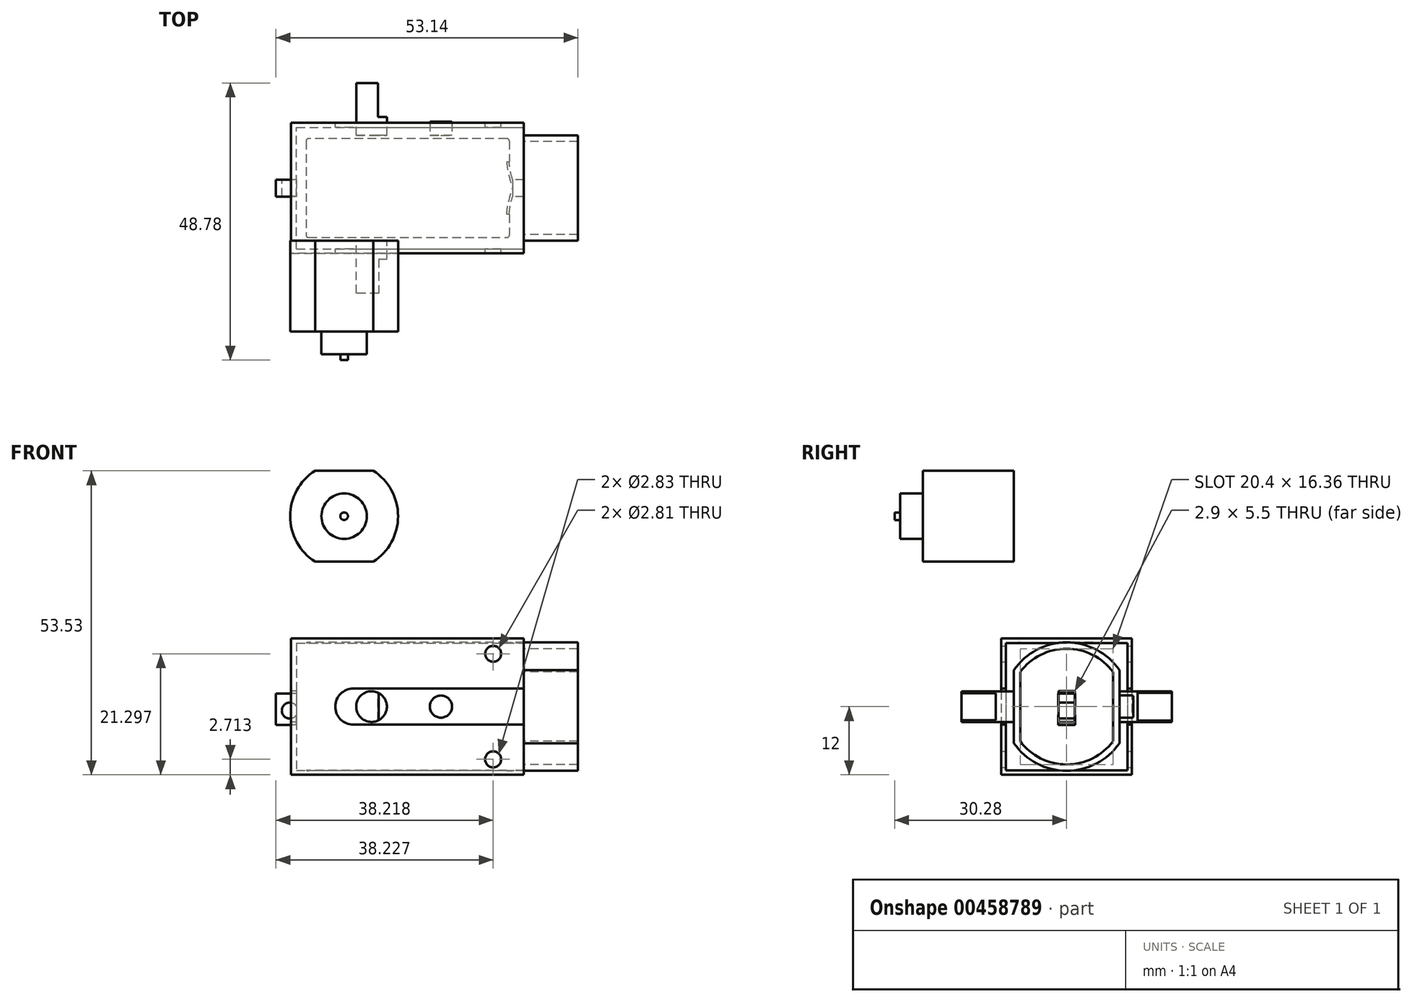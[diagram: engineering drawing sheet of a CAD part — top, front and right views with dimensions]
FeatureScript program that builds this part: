
annotation { "Feature Type Name" : "Feature", "Feature Type Description" : "" }
export const myFeature = defineFeature(function(context is Context, id is Id, definition is map)
    precondition{}
    {
        {
            var Q0;
            Q0=qCreatedBy(makeId("Front.planeOp"),FACE);
            var sketch = newSketch(context, id + "F0", { "sketchPlane" : qUnion([Q0])});
            skLineSegment(sketch, "E0.bottom", {"start": v(-10.04, -11.3) * mm, "end": v(-46.94, -11.3) * mm});
            skLineSegment(sketch, "E0.top", {"start": v(-10.04, 11.3) * mm, "end": v(-46.94, 11.3) * mm});
            skLineSegment(sketch, "E0.right", {"start": v(-46.94, -11.3) * mm, "end": v(-46.94, 11.3) * mm});
            skPoint(sketch, "E0.middle", {"position": v(-20.83, 0) * mm});
            skPoint(sketch, "E1.middle", {"position": v(8.58, 0) * mm});
            skCircle(sketch, "E2", {"center": v(-34.86, 0) * mm, "radius": 2.7 * mm});
            skLineSegment(sketch, "E3.bottom", {"start": v(-46.94, -3.26) * mm, "end": v(-51.68, -3.26) * mm});
            skLineSegment(sketch, "E3.top", {"start": v(-46.94, 2.31) * mm, "end": v(-51.68, 2.31) * mm});
            skLineSegment(sketch, "E3.left", {"start": v(-46.94, -3.26) * mm, "end": v(-46.94, 2.31) * mm});
            skLineSegment(sketch, "E3.right", {"start": v(-51.68, -3.26) * mm, "end": v(-51.68, 2.31) * mm});
            skCircle(sketch, "E4", {"center": v(-49.25, -0.7) * mm, "radius": 1.4 * mm});
            skLineSegment(sketch, "E5", {"start": v(-10.04, 11.3) * mm, "end": v(-10.04, -11.3) * mm});
            skPoint(sketch, "E6.orphan", {"position": v(5.29, 11.3) * mm});
            skPoint(sketch, "E7.orphan", {"position": v(5.29, -11.3) * mm});
            skCircle(sketch, "E8", {"center": v(-13.3, 8.7) * mm, "radius": 1.4 * mm});
            skCircle(sketch, "E9.MirrorC", {"center": v(-13.3, -8.7) * mm, "radius": 1.4 * mm});
            skSolve(sketch);
        }
        {
            var Q0;
            {var subQ9=sQuery(id+"F0.wireOp",EDGE,"E0.bottom");Q0=makeQuery(id+"F0.imprint","IMPRINT",FACE,{"disambiguationData":[TD([[makeQuery(id+"F0.imprint","IMPRINT",EDGE,{"derivedFrom":subQ9}),-1.0]])]});}
            var Q1;
            {var subQ5=sQuery(id+"F0.wireOp",EDGE,"E1.left");Q1=makeQuery(id+"F0.imprint","IMPRINT",FACE,{"disambiguationData":[TD([[makeQuery(id+"F0.imprint","IMPRINT",EDGE,{"derivedFrom":subQ5}),1.0]])]});}
            var Q2;
            {var subQ5=sQuery(id+"F0.wireOp",EDGE,"E1.right");Q2=makeQuery(id+"F0.imprint","IMPRINT",FACE,{"disambiguationData":[TD([[makeQuery(id+"F0.imprint","IMPRINT",EDGE,{"derivedFrom":subQ5}),-1.0]])]});}
            extrude(context, id + "F1", {"entities" : qUnion([Q0, Q1, Q2]), "depth" : 18.56 * mm, "symmetric" : true});
        }
        {
            var Q0;
            Q0=makeQuery(id+"F1.opExtrude","SWEPT_FACE",FACE,{"disambiguationData":[OSD([sQuery(id+"F0.wireOp",EDGE,"E5")])]});
            var sketch = newSketch(context, id + "F2", { "sketchPlane" : qUnion([Q0])});
            skArc(sketch, "E10", {"start": v(-9.28, -6.45) * mm, "mid": v(0, -11.3) * mm, "end": v(9.28, -6.45) * mm});
            skLineSegment(sketch, "E11.0", {"start": v(-9.28, 6.45) * mm, "end": v(-9.28, -6.45) * mm});
            skLineSegment(sketch, "E11.1", {"start": v(9.28, 6.45) * mm, "end": v(9.28, -6.45) * mm});
            skArc(sketch, "E12.trimOffspring", {"start": v(9.28, 6.45) * mm, "mid": v(0, 11.3) * mm, "end": v(-9.28, 6.45) * mm});
            skPoint(sketch, "E13.orphan", {"position": v(-9.28, 11.3) * mm});
            skPoint(sketch, "E14.orphan", {"position": v(-9.28, -11.3) * mm});
            skPoint(sketch, "E15.orphan", {"position": v(9.28, -11.3) * mm});
            skPoint(sketch, "E16.orphan", {"position": v(9.28, 11.3) * mm});
            skArc(sketch, "E17.0", {"start": v(8.18, 6.1) * mm, "mid": v(0, 10.2) * mm, "end": v(-8.18, 6.1) * mm});
            skLineSegment(sketch, "E17.1", {"start": v(8.18, 6.1) * mm, "end": v(8.18, -6.1) * mm});
            skArc(sketch, "E17.2", {"start": v(-8.18, -6.1) * mm, "mid": v(0, -10.2) * mm, "end": v(8.18, -6.1) * mm});
            skLineSegment(sketch, "E17.3", {"start": v(-8.18, 6.1) * mm, "end": v(-8.18, -6.1) * mm});
            skSolve(sketch);
        }
        {
            var Q0;
            {var subQ1=sQuery(id+"F2.wireOp",EDGE,"E11.0");Q0=makeQuery(id+"F2.imprint","IMPRINT",FACE,{"disambiguationData":[TD([[makeQuery(id+"F2.imprint","IMPRINT",EDGE,{"derivedFrom":subQ1}),1.0]])]});}
            extrude(context, id + "F3", {"entities" : qUnion([Q0]), "operationType" : NewBodyOperationType.ADD, "depth" : 11.5 * mm});
        }
        {
            var Q0;
            Q0=makeQuery(id+"F0.imprint","IMPRINT",FACE,{"disambiguationData":[TD([[makeQuery(id+"F0.imprint","IMPRINT",EDGE,{"derivedFrom":sQuery(id+"F0.wireOp",EDGE,"E3.bottom")}),-1.0]])]});
            extrude(context, id + "F4", {"entities" : qUnion([Q0]), "operationType" : NewBodyOperationType.ADD, "depth" : 3 * mm, "offsetDistance" : 25 * mm, "symmetric" : true});
        }
        {
            var Q0;
            Q0=makeQuery(id+"F0.imprint","IMPRINT",FACE,{"disambiguationData":[TD([[makeQuery(id+"F0.imprint","IMPRINT",EDGE,{"derivedFrom":sQuery(id+"F0.wireOp",EDGE,"E2")}),1.0]])]});
            extrude(context, id + "F5", {"entities" : qUnion([Q0]), "depth" : 37 * mm, "symmetric" : true});
        }
        {
            var Q0;
            Q0=makeQuery(id+"F5.opExtrude","CAP_FACE",FACE,{"disambiguationData":[OSD([sQuery(id+"F0.wireOp",EDGE,"E2")])],"isStart":false});
            var sketch = newSketch(context, id + "F6", { "sketchPlane" : qUnion([Q0])});
            skCircle(sketch, "E18.0.0", {"center": v(-34.86, 0) * mm, "radius": 2.7 * mm});
            skLineSegment(sketch, "E19", {"start": v(-33.6, 2.39) * mm, "end": v(-33.6, -2.39) * mm});
            skSolve(sketch);
        }
        {
            var Q0;
            {var subQ0=sQuery(id+"F6.wireOp",EDGE,"E19");Q0=makeQuery(id+"F6.imprint","IMPRINT",FACE,{"disambiguationData":[TD([[makeQuery(id+"F6.imprint","IMPRINT",EDGE,{"derivedFrom":subQ0}),1.0]])]});}
            extrude(context, id + "F7", {"entities" : qUnion([Q0]), "operationType" : NewBodyOperationType.REMOVE, "oppositeDirection" : true, "depth" : 6 * mm});
        }
        {
            var Q0;
            Q0=makeQuery(id+"F5.opExtrude","CAP_FACE",FACE,{"disambiguationData":[OSD([sQuery(id+"F0.wireOp",EDGE,"E2")])],"isStart":true});
            var sketch = newSketch(context, id + "F8", { "sketchPlane" : qUnion([Q0])});
            skLineSegment(sketch, "E20", {"start": v(33.7, -2.44) * mm, "end": v(33.7, 2.44) * mm});
            skSolve(sketch);
        }
        {
            var Q0;
            {var subQ0=sQuery(id+"F8.wireOp",EDGE,"E20");Q0=makeQuery(id+"F8.imprint","IMPRINT",FACE,{"disambiguationData":[TD([[makeQuery(id+"F8.imprint","IMPRINT",EDGE,{"derivedFrom":subQ0}),1.0]])]});}
            extrude(context, id + "F9", {"entities" : qUnion([Q0]), "operationType" : NewBodyOperationType.REMOVE, "oppositeDirection" : true, "depth" : 6 * mm});
        }
        {
            var Q0;
            Q0=makeQuery(id+"F3.boolean.opBoolean","MERGE",FACE,{"derivedFrom":[makeQuery(id+"F1.opExtrude","CAP_FACE",FACE,{"disambiguationData":[OSD([sQuery(id+"F0.wireOp",EDGE,"E0.bottom"),sQuery(id+"F0.wireOp",EDGE,"E0.top"),sQuery(id+"F0.wireOp",EDGE,"E0.right"),sQuery(id+"F0.wireOp",EDGE,"E2"),sQuery(id+"F0.wireOp",EDGE,"E3.left"),sQuery(id+"F0.wireOp",EDGE,"E5"),sQuery(id+"F0.wireOp",EDGE,"E8"),sQuery(id+"F0.wireOp",EDGE,"E9.MirrorC")])],"isStart":false}),makeQuery(id+"F3.opExtrude","SWEPT_FACE",FACE,{"disambiguationData":[OSD([sQuery(id+"F2.wireOp",EDGE,"E11.0")])]})]});
            var sketch = newSketch(context, id + "F10", { "sketchPlane" : qUnion([Q0])});
            skArc(sketch, "E21", {"start": v(-44.8, 41.53) * mm, "mid": v(-49.18, 33.53) * mm, "end": v(-44.8, 25.53) * mm});
            skLineSegment(sketch, "E22.bottom", {"start": v(-44.8, 41.53) * mm, "end": v(-34.56, 41.53) * mm});
            skLineSegment(sketch, "E22.top", {"start": v(-44.8, 25.53) * mm, "end": v(-34.56, 25.53) * mm});
            skArc(sketch, "E23.trimOffspring", {"start": v(-34.56, 25.53) * mm, "mid": v(-30.18, 33.53) * mm, "end": v(-34.56, 41.53) * mm});
            skSolve(sketch);
        }
        {
            var Q0;
            Q0=qSketchRegion(id+"F10",true);
            extrude(context, id + "F11", {"entities" : qUnion([Q0]), "depth" : 16 * mm});
        }
        {
            var Q0;
            Q0=makeQuery(id+"F11.opExtrude","CAP_FACE",FACE,{"disambiguationData":[OSD([sQuery(id+"F10.wireOp",EDGE,"E21"),sQuery(id+"F10.wireOp",EDGE,"E22.bottom"),sQuery(id+"F10.wireOp",EDGE,"E22.top"),sQuery(id+"F10.wireOp",EDGE,"E23.trimOffspring")])],"isStart":false});
            var sketch = newSketch(context, id + "F12", { "sketchPlane" : qUnion([Q0])});
            skCircle(sketch, "E24", {"center": v(-39.68, 33.53) * mm, "radius": 4 * mm});
            skCircle(sketch, "E25", {"center": v(-39.68, 33.53) * mm, "radius": 0.67 * mm});
            skSolve(sketch);
        }
        {
            var Q0;
            Q0=makeQuery(id+"F12.imprint","IMPRINT",FACE,{"disambiguationData":[TD([[makeQuery(id+"F12.imprint","IMPRINT",EDGE,{"derivedFrom":sQuery(id+"F12.wireOp",EDGE,"E24")}),1.0]])]});
            extrude(context, id + "F13", {"entities" : qUnion([Q0]), "operationType" : NewBodyOperationType.ADD, "depth" : 4 * mm});
        }
        {
            var Q0;
            Q0=makeQuery(id+"F13.boolean.opBoolean","SPLIT",FACE,{"disambiguationData":[TD([makeQuery(id+"F13.opExtrude","SWEPT_FACE",FACE,{"disambiguationData":[OSD([sQuery(id+"F12.wireOp",EDGE,"E25")])]})])],"derivedFrom":makeQuery(id+"F11.opExtrude","CAP_FACE",FACE,{"disambiguationData":[OSD([sQuery(id+"F10.wireOp",EDGE,"E21"),sQuery(id+"F10.wireOp",EDGE,"E22.bottom"),sQuery(id+"F10.wireOp",EDGE,"E22.top"),sQuery(id+"F10.wireOp",EDGE,"E23.trimOffspring")])],"isStart":false})});
            extrude(context, id + "F14", {"entities" : qUnion([Q0]), "operationType" : NewBodyOperationType.ADD, "depth" : 5 * mm});
        }
        {
            var Q0;
            Q0=makeQuery(id+"F1.opExtrude","CAP_EDGE",EDGE,{"disambiguationData":[OSD([sQuery(id+"F0.wireOp",EDGE,"E0.top")])],"isStart":false});
            var Q1;
            {var subQ0=sQuery(id+"F0.wireOp",EDGE,"E5");var subQ1=sQuery(id+"F0.wireOp",EDGE,"E0.top");Q1=makeQuery(id+"F3.boolean.opBoolean","SPLIT",EDGE,{"disambiguationData":[TD([makeQuery(id+"F3.opExtrude","SWEPT_FACE",FACE,{"disambiguationData":[OSD([sQuery(id+"F2.wireOp",EDGE,"E11.0")])]})])],"derivedFrom":makeQuery(id+"F1.opExtrude","SWEPT_EDGE",EDGE,{"disambiguationData":[OSD([subQ1,subQ0])]})});}
            var Q2;
            {var subQ0=sQuery(id+"F0.wireOp",EDGE,"E0.top");var subQ1=sQuery(id+"F0.wireOp",EDGE,"E5");Q2=makeQuery(id+"F3.boolean.opBoolean","SPLIT",EDGE,{"disambiguationData":[TD([makeQuery(id+"F3.opExtrude","SWEPT_FACE",FACE,{"disambiguationData":[OSD([sQuery(id+"F2.wireOp",EDGE,"E11.1")])]})])],"derivedFrom":makeQuery(id+"F1.opExtrude","SWEPT_EDGE",EDGE,{"disambiguationData":[OSD([subQ0,subQ1])]})});}
            var Q3;
            Q3=makeQuery(id+"F1.opExtrude","CAP_EDGE",EDGE,{"disambiguationData":[OSD([sQuery(id+"F0.wireOp",EDGE,"E0.top")])],"isStart":true});
            var Q4;
            Q4=makeQuery(id+"F1.opExtrude","SWEPT_EDGE",EDGE,{"disambiguationData":[OSD([sQuery(id+"F0.wireOp",EDGE,"E0.top"),sQuery(id+"F0.wireOp",EDGE,"E0.right")])]});
            var Q5;
            Q5=makeQuery(id+"F1.opExtrude","CAP_EDGE",EDGE,{"disambiguationData":[OSD([sQuery(id+"F0.wireOp",EDGE,"E0.right"),sQuery(id+"F0.wireOp",EDGE,"E3.left")])],"isStart":true});
            var Q6;
            Q6=makeQuery(id+"F1.opExtrude","CAP_EDGE",EDGE,{"disambiguationData":[OSD([sQuery(id+"F0.wireOp",EDGE,"E0.bottom")])],"isStart":true});
            var Q7;
            {var subQ0=sQuery(id+"F0.wireOp",EDGE,"E5");var subQ1=sQuery(id+"F0.wireOp",EDGE,"E0.bottom");Q7=makeQuery(id+"F3.boolean.opBoolean","SPLIT",EDGE,{"disambiguationData":[TD([makeQuery(id+"F1.opExtrude","SWEPT_FACE",FACE,{"disambiguationData":[OSD([subQ1])]})])],"derivedFrom":makeQuery(id+"F1.opExtrude","CAP_EDGE",EDGE,{"disambiguationData":[OSD([subQ0])],"isStart":true})});}
            var Q8;
            {var subQ0=sQuery(id+"F0.wireOp",EDGE,"E0.top");var subQ1=sQuery(id+"F0.wireOp",EDGE,"E5");Q8=makeQuery(id+"F3.boolean.opBoolean","SPLIT",EDGE,{"disambiguationData":[TD([makeQuery(id+"F1.opExtrude","SWEPT_FACE",FACE,{"disambiguationData":[OSD([subQ0])]})])],"derivedFrom":makeQuery(id+"F1.opExtrude","CAP_EDGE",EDGE,{"disambiguationData":[OSD([subQ1])],"isStart":true})});}
            var Q9;
            Q9=makeQuery(id+"F1.opExtrude","CAP_EDGE",EDGE,{"disambiguationData":[OSD([sQuery(id+"F0.wireOp",EDGE,"E0.right"),sQuery(id+"F0.wireOp",EDGE,"E3.left")])],"isStart":false});
            var Q10;
            Q10=makeQuery(id+"F1.opExtrude","SWEPT_EDGE",EDGE,{"disambiguationData":[OSD([sQuery(id+"F0.wireOp",EDGE,"E0.bottom"),sQuery(id+"F0.wireOp",EDGE,"E0.right")])]});
            var Q11;
            Q11=makeQuery(id+"F1.opExtrude","CAP_EDGE",EDGE,{"disambiguationData":[OSD([sQuery(id+"F0.wireOp",EDGE,"E0.bottom")])],"isStart":false});
            var Q12;
            {var subQ0=sQuery(id+"F0.wireOp",EDGE,"E5");var subQ1=sQuery(id+"F0.wireOp",EDGE,"E0.bottom");Q12=makeQuery(id+"F3.boolean.opBoolean","SPLIT",EDGE,{"disambiguationData":[TD([makeQuery(id+"F3.opExtrude","SWEPT_FACE",FACE,{"disambiguationData":[OSD([sQuery(id+"F2.wireOp",EDGE,"E11.0")])]})])],"derivedFrom":makeQuery(id+"F1.opExtrude","SWEPT_EDGE",EDGE,{"disambiguationData":[OSD([subQ1,subQ0])]})});}
            var Q13;
            {var subQ0=sQuery(id+"F0.wireOp",EDGE,"E5");var subQ1=sQuery(id+"F0.wireOp",EDGE,"E0.bottom");Q13=makeQuery(id+"F3.boolean.opBoolean","SPLIT",EDGE,{"disambiguationData":[TD([makeQuery(id+"F3.opExtrude","SWEPT_FACE",FACE,{"disambiguationData":[OSD([sQuery(id+"F2.wireOp",EDGE,"E11.1")])]})])],"derivedFrom":makeQuery(id+"F1.opExtrude","SWEPT_EDGE",EDGE,{"disambiguationData":[OSD([subQ1,subQ0])]})});}
            fillet(context, id + "F15", {"entities" : qUnion([Q0, Q1, Q2, Q3, Q4, Q5, Q6, Q7, Q8, Q9, Q10, Q11, Q12, Q13]), "radius" : 1 * mm, "tangentPropagation" : true, "allowEdgeOverflow" : false});
        }
        {
            var Q0;
            {var subQ0=sQuery(id+"F0.wireOp",EDGE,"E5");var subQ1=sQuery(id+"F0.wireOp",EDGE,"E0.bottom");Q0=makeQuery(id+"F3.boolean.opBoolean","SPLIT",EDGE,{"disambiguationData":[TD([makeQuery(id+"F1.opExtrude","SWEPT_FACE",FACE,{"disambiguationData":[OSD([subQ1])]})])],"derivedFrom":makeQuery(id+"F1.opExtrude","CAP_EDGE",EDGE,{"disambiguationData":[OSD([subQ0])],"isStart":false})});}
            var Q1;
            {var subQ0=sQuery(id+"F0.wireOp",EDGE,"E5");var subQ1=sQuery(id+"F0.wireOp",EDGE,"E0.top");Q1=makeQuery(id+"F3.boolean.opBoolean","SPLIT",EDGE,{"disambiguationData":[TD([makeQuery(id+"F1.opExtrude","SWEPT_FACE",FACE,{"disambiguationData":[OSD([subQ1])]})])],"derivedFrom":makeQuery(id+"F1.opExtrude","CAP_EDGE",EDGE,{"disambiguationData":[OSD([subQ0])],"isStart":false})});}
            fillet(context, id + "F16", {"entities" : qUnion([Q0, Q1]), "radius" : 1 * mm, "tangentPropagation" : true, "allowEdgeOverflow" : false});
        }
        {
            var Q0;
            Q0=makeQuery(id+"F3.boolean.opBoolean","MERGE",FACE,{"derivedFrom":[makeQuery(id+"F1.opExtrude","CAP_FACE",FACE,{"disambiguationData":[OSD([sQuery(id+"F0.wireOp",EDGE,"E0.bottom"),sQuery(id+"F0.wireOp",EDGE,"E0.top"),sQuery(id+"F0.wireOp",EDGE,"E0.right"),sQuery(id+"F0.wireOp",EDGE,"E2"),sQuery(id+"F0.wireOp",EDGE,"E3.left"),sQuery(id+"F0.wireOp",EDGE,"E5"),sQuery(id+"F0.wireOp",EDGE,"E8"),sQuery(id+"F0.wireOp",EDGE,"E9.MirrorC")])],"isStart":false}),makeQuery(id+"F3.opExtrude","SWEPT_FACE",FACE,{"disambiguationData":[OSD([sQuery(id+"F2.wireOp",EDGE,"E11.0")])]})]});
            var sketch = newSketch(context, id + "F17", { "sketchPlane" : qUnion([Q0])});
            skCircle(sketch, "E26", {"center": v(-22.64, 0) * mm, "radius": 1.95 * mm});
            skSolve(sketch);
        }
        {
            var Q0;
            Q0 = qSketchRegion(id + "F17", true);
            extrude(context, id + "F18", {"entities" : qUnion([Q0]), "operationType" : NewBodyOperationType.ADD, "oppositeDirection" : true, "depth" : 21 * mm, "offsetDistance" : 25 * mm});
        }
        {
            var Q0;
            Q0=makeQuery(id+"F18.opExtrude","CAP_EDGE",EDGE,{"disambiguationData":[OSD([sQuery(id+"F17.wireOp",EDGE,"E26")])],"isStart":false});
            fillet(context, id + "F19", {"entities" : qUnion([Q0]), "radius" : .2 * mm, "tangentPropagation" : true, "allowEdgeOverflow" : false});
        }
        {
            var Q0;
            {var subQ3=sQuery(id+"F0.wireOp",EDGE,"E0.bottom");Q0=makeQuery(id+"F0.imprint","IMPRINT",FACE,{"disambiguationData":[TD([[makeQuery(id+"F0.imprint","IMPRINT",EDGE,{"derivedFrom":subQ3}),-1.0]])]});}
            var sketch = newSketch(context, id + "F20", { "sketchPlane" : qUnion([Q0])});
            skLineSegment(sketch, "E27.2", {"start": v(-49.05, -12) * mm, "end": v(-8.05, -12) * mm});
            skLineSegment(sketch, "E27.5", {"start": v(-8.05, 12) * mm, "end": v(-49.05, 12) * mm});
            skLineSegment(sketch, "E28", {"start": v(-38.06, 3.19) * mm, "end": v(-8.05, 3.19) * mm});
            skLineSegment(sketch, "E29.MirrorCS", {"start": v(-38.06, -3.19) * mm, "end": v(-8.05, -3.19) * mm});
            skLineSegment(sketch, "E30", {"start": v(-8.05, 12) * mm, "end": v(-8.05, 3.19) * mm});
            skLineSegment(sketch, "E31", {"start": v(-8.05, -3.19) * mm, "end": v(-8.05, -12) * mm});
            skCircle(sketch, "E32", {"center": v(-13.45, 9.3) * mm, "radius": 1.4 * mm});
            skCircle(sketch, "E33", {"center": v(-13.46, -9.29) * mm, "radius": 1.41 * mm});
            skArc(sketch, "E34", {"start": v(-38.06, 3.19) * mm, "mid": v(-41.25, 0) * mm, "end": v(-38.06, -3.19) * mm});
            skLineSegment(sketch, "E35", {"start": v(-49.05, 12) * mm, "end": v(-49.05, 0) * mm});
            skPoint(sketch, "E35.endSnap0", {"position": v(-41.25, 0) * mm});
            skLineSegment(sketch, "E36", {"start": v(-49.05, 0) * mm, "end": v(-49.05, -12) * mm});
            skSolve(sketch);
        }
        {
            var Q0;
            Q0 = qSketchRegion(id + "F20", true);
            extrude(context, id + "F21", {"entities" : qUnion([Q0]), "depth" : 23 * mm, "offsetDistance" : 25 * mm, "symmetric" : true});
        }
        {
            var Q0;
            Q0=makeQuery(id+"F21.opExtrude","SWEPT_FACE",FACE,{"disambiguationData":[OSD([sQuery(id+"F20.wireOp",EDGE,"E30")])]});
            var sketch = newSketch(context, id + "F22", { "sketchPlane" : qUnion([Q0])});
            skLineSegment(sketch, "E37.0", {"start": v(10.7, 11.2) * mm, "end": v(10.7, 3.02) * mm});
            skLineSegment(sketch, "E37.1", {"start": v(-10.7, 11.2) * mm, "end": v(10.7, 11.2) * mm});
            skLineSegment(sketch, "E37.2", {"start": v(-10.7, 11.2) * mm, "end": v(-10.7, 3.02) * mm});
            skLineSegment(sketch, "E38.0", {"start": v(10.7, -3.02) * mm, "end": v(10.7, -11.2) * mm});
            skLineSegment(sketch, "E38.1", {"start": v(-10.7, -11.2) * mm, "end": v(10.7, -11.2) * mm});
            skLineSegment(sketch, "E38.2", {"start": v(-10.7, -3.02) * mm, "end": v(-10.7, -11.2) * mm});
            skLineSegment(sketch, "E39", {"start": v(-10.7, 3.02) * mm, "end": v(10.7, 3.02) * mm});
            skLineSegment(sketch, "E40", {"start": v(10.7, -3.02) * mm, "end": v(-10.7, -3.02) * mm});
            skSolve(sketch);
        }
        {
            var Q0;
            {var subQ0=sQuery(id+"F22.wireOp",EDGE,"E37.1");Q0=makeQuery(id+"F22.imprint","IMPRINT",FACE,{"disambiguationData":[TD([[makeQuery(id+"F22.imprint","IMPRINT",EDGE,{"derivedFrom":subQ0}),-1.0]])]});}
            var Q1;
            Q1=makeQuery(id+"F22.imprint","IMPRINT",FACE,{"disambiguationData":[TD([[makeQuery(id+"F22.imprint","IMPRINT",EDGE,{"derivedFrom":sQuery(id+"F22.wireOp",EDGE,"E39")}),-1.0]])]});
            var Q2;
            Q2=makeQuery(id+"F22.imprint","IMPRINT",FACE,{"disambiguationData":[TD([[makeQuery(id+"F22.imprint","IMPRINT",EDGE,{"derivedFrom":sQuery(id+"F22.wireOp",EDGE,"E38.0")}),-1.0]])]});
            extrude(context, id + "F23", {"entities" : qUnion([Q0, Q1, Q2]), "operationType" : NewBodyOperationType.REMOVE, "oppositeDirection" : true, "depth" : 40 * mm, "offsetDistance" : 25 * mm});
        }
        {
            var Q0;
            Q0=makeQuery(id+"F23.boolean.opBoolean","COPY",FACE,{"derivedFrom":makeQuery(id+"F23.opExtrude","SWEPT_FACE",FACE,{"disambiguationData":[OSD([sQuery(id+"F20.wireOp",EDGE,"E28"),sQuery(id+"F20.wireOp",EDGE,"E30")])]})});
            extrude(context, id + "F24", {"entities" : qUnion([Q0]), "operationType" : NewBodyOperationType.REMOVE, "oppositeDirection" : true, "depth" : 4 * mm, "offsetDistance" : 25 * mm});
        }
        {
            var Q0;
            Q0=makeQuery(id+"F23.boolean.opBoolean","COPY",FACE,{"derivedFrom":makeQuery(id+"F23.opExtrude","SWEPT_FACE",FACE,{"disambiguationData":[OSD([sQuery(id+"F22.wireOp",EDGE,"E40")])]})});
            extrude(context, id + "F25", {"entities" : qUnion([Q0]), "operationType" : NewBodyOperationType.REMOVE, "oppositeDirection" : true, "depth" : 10 * mm, "offsetDistance" : 25 * mm});
        }
        {
            var Q0;
            Q0=makeQuery(id+"F21.opExtrude","SWEPT_FACE",FACE,{"disambiguationData":[OSD([sQuery(id+"F20.wireOp",EDGE,"E35"),sQuery(id+"F20.wireOp",EDGE,"E36")])]});
            var sketch = newSketch(context, id + "F26", { "sketchPlane" : qUnion([Q0])});
            skLineSegment(sketch, "E41.bottom", {"start": v(1.45, -2.75) * mm, "end": v(-1.45, -2.75) * mm});
            skLineSegment(sketch, "E41.top", {"start": v(1.45, 2.75) * mm, "end": v(-1.45, 2.75) * mm});
            skLineSegment(sketch, "E41.left", {"start": v(1.45, -2.75) * mm, "end": v(1.45, 2.75) * mm});
            skLineSegment(sketch, "E41.right", {"start": v(-1.45, -2.75) * mm, "end": v(-1.45, 2.75) * mm});
            skPoint(sketch, "E41.middle", {"position": v(0, 0) * mm});
            skSolve(sketch);
        }
        {
            var Q0;
            Q0=makeQuery(id+"F26.imprint","IMPRINT",FACE,{"disambiguationData":[TD([[makeQuery(id+"F26.imprint","IMPRINT",EDGE,{"derivedFrom":sQuery(id+"F26.wireOp",EDGE,"E41.bottom")}),-1.0]])]});
            extrude(context, id + "F27", {"entities" : qUnion([Q0]), "operationType" : NewBodyOperationType.REMOVE, "oppositeDirection" : true, "depth" : 25 * mm, "offsetDistance" : 25 * mm});
        }
    });
